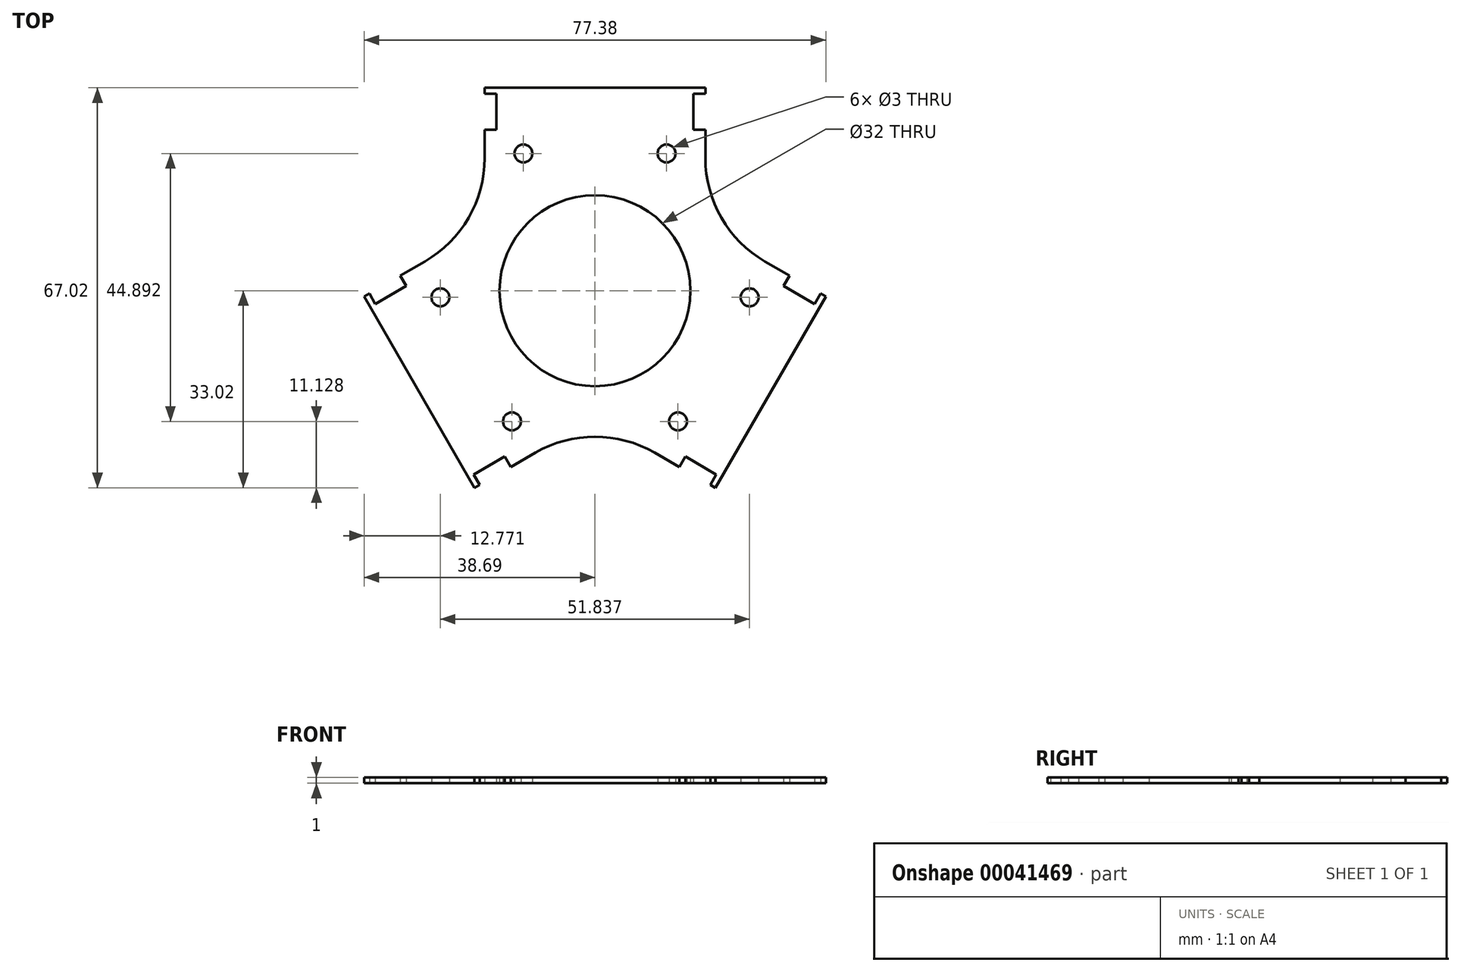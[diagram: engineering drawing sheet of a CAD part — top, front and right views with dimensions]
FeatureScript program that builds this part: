
annotation { "Feature Type Name" : "Feature", "Feature Type Description" : "" }
export const myFeature = defineFeature(function(context is Context, id is Id, definition is map)
    precondition{}
    {
        {
            var Q0;
            Q0=qCreatedBy(makeId("Top.planeOp"),FACE);
            var sketch = newSketch(context, id + "F0", { "sketchPlane" : qUnion([Q0])});
            skLineSegment(sketch, "E0", {"start": v(0, 0) * mm, "end": v(25.98, -15) * mm, "construction": true});
            skLineSegment(sketch, "E1", {"start": v(38.98, 7.52) * mm, "end": v(12.98, -37.52) * mm, "construction": true});
            skLineSegment(sketch, "E2", {"start": v(36.23, 2.75) * mm, "end": v(15.73, -32.75) * mm, "construction": true});
            skLineSegment(sketch, "E3", {"start": v(15.73, -32.75) * mm, "end": v(17.73, -29.29) * mm, "construction": true});
            skLineSegment(sketch, "E4", {"start": v(18.33, -34.25) * mm, "end": v(13.13, -31.25) * mm, "construction": true});
            skLineSegment(sketch, "E5", {"start": v(18.33, -34.25) * mm, "end": v(20.33, -30.79) * mm});
            skLineSegment(sketch, "E6", {"start": v(20.33, -30.79) * mm, "end": v(17.73, -29.29) * mm});
            skLineSegment(sketch, "E7", {"start": v(19.33, -32.52) * mm, "end": v(20.2, -33.02) * mm});
            skLineSegment(sketch, "E8", {"start": v(20.2, -33.02) * mm, "end": v(38.7, -0.98) * mm});
            skLineSegment(sketch, "E9", {"start": v(13.13, -31.25) * mm, "end": v(15.13, -27.79) * mm});
            skLineSegment(sketch, "E10", {"start": v(15.13, -27.79) * mm, "end": v(17.73, -29.29) * mm});
            skLineSegment(sketch, "E11.MirrorCS", {"start": v(37.83, -0.48) * mm, "end": v(38.7, -0.98) * mm});
            skLineSegment(sketch, "E12.MirrorCS", {"start": v(38.83, 1.25) * mm, "end": v(36.83, -2.21) * mm});
            skLineSegment(sketch, "E13.MirrorCS", {"start": v(36.83, -2.21) * mm, "end": v(34.23, -0.71) * mm});
            skLineSegment(sketch, "E14.MirrorCS", {"start": v(38.83, 1.25) * mm, "end": v(33.63, 4.25) * mm, "construction": true});
            skLineSegment(sketch, "E15.MirrorCS", {"start": v(31.63, 0.79) * mm, "end": v(34.23, -0.71) * mm});
            skLineSegment(sketch, "E16.MirrorCS", {"start": v(33.63, 4.25) * mm, "end": v(31.63, 0.79) * mm});
            skLineSegment(sketch, "E17", {"start": v(-20.5, 30) * mm, "end": v(20.5, 30) * mm, "construction": true});
            skLineSegment(sketch, "E18", {"start": v(0, 0) * mm, "end": v(0, 30) * mm, "construction": true});
            skLineSegment(sketch, "E19", {"start": v(-26, 30) * mm, "end": v(26, 30) * mm, "construction": true});
            skLineSegment(sketch, "E20", {"start": v(18.5, 34) * mm, "end": v(-18.5, 34) * mm});
            skLineSegment(sketch, "E21.MirrorCS", {"start": v(-20.5, 33) * mm, "end": v(-20.5, 27) * mm, "construction": true});
            skLineSegment(sketch, "E22", {"start": v(20.5, 33) * mm, "end": v(20.5, 27) * mm, "construction": true});
            skLineSegment(sketch, "E23.MirrorCS", {"start": v(-16.5, 33) * mm, "end": v(-16.5, 30) * mm});
            skLineSegment(sketch, "E24", {"start": v(16.5, 33) * mm, "end": v(16.5, 30) * mm});
            skLineSegment(sketch, "E25.MirrorCS", {"start": v(-20.5, 27) * mm, "end": v(-16.5, 27) * mm});
            skLineSegment(sketch, "E26", {"start": v(20.5, 27) * mm, "end": v(16.5, 27) * mm});
            skLineSegment(sketch, "E27.MirrorCS", {"start": v(-16.5, 27) * mm, "end": v(-16.5, 30) * mm});
            skLineSegment(sketch, "E28", {"start": v(16.5, 27) * mm, "end": v(16.5, 30) * mm});
            skLineSegment(sketch, "E29.MirrorCS", {"start": v(-18.5, 33) * mm, "end": v(-18.5, 34) * mm});
            skLineSegment(sketch, "E30.MirrorCS", {"start": v(-20.5, 33) * mm, "end": v(-16.5, 33) * mm});
            skLineSegment(sketch, "E31", {"start": v(20.5, 30) * mm, "end": v(16.5, 30) * mm, "construction": true});
            skLineSegment(sketch, "E32", {"start": v(18.5, 33) * mm, "end": v(18.5, 34) * mm});
            skLineSegment(sketch, "E33", {"start": v(20.5, 33) * mm, "end": v(16.5, 33) * mm});
            skLineSegment(sketch, "E34", {"start": v(-15.73, -32.75) * mm, "end": v(-36.23, 2.75) * mm, "construction": true});
            skLineSegment(sketch, "E35", {"start": v(0, 0) * mm, "end": v(-25.98, -15) * mm, "construction": true});
            skLineSegment(sketch, "E36", {"start": v(-12.98, -37.52) * mm, "end": v(-38.98, 7.52) * mm, "construction": true});
            skLineSegment(sketch, "E37", {"start": v(-38.7, -0.98) * mm, "end": v(-20.2, -33.02) * mm});
            skLineSegment(sketch, "E38.MirrorCS", {"start": v(-18.33, -34.25) * mm, "end": v(-13.13, -31.25) * mm, "construction": true});
            skLineSegment(sketch, "E39", {"start": v(-38.83, 1.25) * mm, "end": v(-33.63, 4.25) * mm, "construction": true});
            skLineSegment(sketch, "E40.MirrorCS", {"start": v(-20.33, -30.79) * mm, "end": v(-17.73, -29.29) * mm});
            skLineSegment(sketch, "E41", {"start": v(-36.83, -2.21) * mm, "end": v(-34.23, -0.71) * mm});
            skLineSegment(sketch, "E42.MirrorCS", {"start": v(-13.13, -31.25) * mm, "end": v(-15.13, -27.79) * mm});
            skLineSegment(sketch, "E43", {"start": v(-33.63, 4.25) * mm, "end": v(-31.63, 0.79) * mm});
            skLineSegment(sketch, "E44.MirrorCS", {"start": v(-15.13, -27.79) * mm, "end": v(-17.73, -29.29) * mm});
            skLineSegment(sketch, "E45", {"start": v(-31.63, 0.79) * mm, "end": v(-34.23, -0.71) * mm});
            skLineSegment(sketch, "E46.MirrorCS", {"start": v(-19.33, -32.52) * mm, "end": v(-20.2, -33.02) * mm});
            skLineSegment(sketch, "E47.MirrorCS", {"start": v(-18.33, -34.25) * mm, "end": v(-20.33, -30.79) * mm});
            skLineSegment(sketch, "E48", {"start": v(-36.23, 2.75) * mm, "end": v(-34.23, -0.71) * mm, "construction": true});
            skLineSegment(sketch, "E49", {"start": v(-37.83, -0.48) * mm, "end": v(-38.7, -0.98) * mm});
            skLineSegment(sketch, "E50", {"start": v(-38.83, 1.25) * mm, "end": v(-36.83, -2.21) * mm});
            skLineSegment(sketch, "E51", {"start": v(18.5, 27) * mm, "end": v(18.5, 26) * mm});
            skLineSegment(sketch, "E52", {"start": v(32.63, 2.52) * mm, "end": v(31.77, 3.02) * mm});
            skLineSegment(sketch, "E53", {"start": v(18.5, 26) * mm, "end": v(18.5, 22.23) * mm});
            skLineSegment(sketch, "E54", {"start": v(28.5, 4.9) * mm, "end": v(31.77, 3.02) * mm});
            skLineSegment(sketch, "E55", {"start": v(-32.63, 2.52) * mm, "end": v(-31.77, 3.02) * mm});
            skLineSegment(sketch, "E56", {"start": v(-31.77, 3.02) * mm, "end": v(-28.5, 4.9) * mm});
            skLineSegment(sketch, "E57", {"start": v(-18.5, 22.23) * mm, "end": v(-18.5, 26) * mm});
            skLineSegment(sketch, "E58", {"start": v(-18.5, 26) * mm, "end": v(-18.5, 27) * mm});
            skLineSegment(sketch, "E59", {"start": v(-14.13, -29.52) * mm, "end": v(-13.27, -29.02) * mm});
            skLineSegment(sketch, "E60", {"start": v(-13.27, -29.02) * mm, "end": v(-10, -27.14) * mm});
            skLineSegment(sketch, "E61", {"start": v(10, -27.14) * mm, "end": v(13.27, -29.02) * mm});
            skLineSegment(sketch, "E62", {"start": v(14.13, -29.52) * mm, "end": v(13.27, -29.02) * mm});
            skPoint(sketch, "E63.visualSharp", {"position": v(18.5, 10.68) * mm});
            skArc(sketch, "E63.filletArc", {"start": v(18.5, 22.23) * mm, "mid": v(21.18, 12.23) * mm, "end": v(28.5, 4.9) * mm});
            skPoint(sketch, "E64.visualSharp", {"position": v(0, -21.36) * mm});
            skArc(sketch, "E64.filletArc", {"start": v(10, -27.14) * mm, "mid": v(0, -24.46) * mm, "end": v(-10, -27.14) * mm});
            skPoint(sketch, "E65.visualSharp", {"position": v(-18.5, 10.68) * mm});
            skArc(sketch, "E65.filletArc", {"start": v(-28.5, 4.9) * mm, "mid": v(-21.18, 12.23) * mm, "end": v(-18.5, 22.23) * mm});
            skCircle(sketch, "E66", {"center": v(0, 0) * mm, "radius": 16 * mm});
            skLineSegment(sketch, "E67", {"start": v(0, 30) * mm, "end": v(0, 23) * mm, "construction": true});
            skLineSegment(sketch, "E68", {"start": v(-12, 23) * mm, "end": v(12, 23) * mm, "construction": true});
            skCircle(sketch, "E69", {"center": v(-12, 23) * mm, "radius": 1.5 * mm});
            skCircle(sketch, "E70", {"center": v(12, 23) * mm, "radius": 1.5 * mm});
            skLineSegment(sketch, "E71", {"start": v(25.98, -15) * mm, "end": v(19.92, -11.5) * mm, "construction": true});
            skLineSegment(sketch, "E72", {"start": v(-25.98, -15) * mm, "end": v(-19.92, -11.5) * mm, "construction": true});
            skLineSegment(sketch, "E73", {"start": v(25.92, -1.1) * mm, "end": v(13.92, -21.9) * mm, "construction": true});
            skLineSegment(sketch, "E74", {"start": v(-25.92, -1.1) * mm, "end": v(-13.92, -21.9) * mm, "construction": true});
            skCircle(sketch, "E75", {"center": v(25.92, -1.1) * mm, "radius": 1.5 * mm});
            skCircle(sketch, "E76", {"center": v(13.92, -21.9) * mm, "radius": 1.5 * mm});
            skCircle(sketch, "E77", {"center": v(-13.92, -21.9) * mm, "radius": 1.5 * mm});
            skCircle(sketch, "E78", {"center": v(-25.92, -1.1) * mm, "radius": 1.5 * mm});
            skSolve(sketch);
        }
        {
            var Q0;
            Q0 = qSketchRegion(id + "F0", true);
            extrude(context, id + "F1", {"entities" : qUnion([Q0]), "depth" : 1 * mm});
        }
    });
